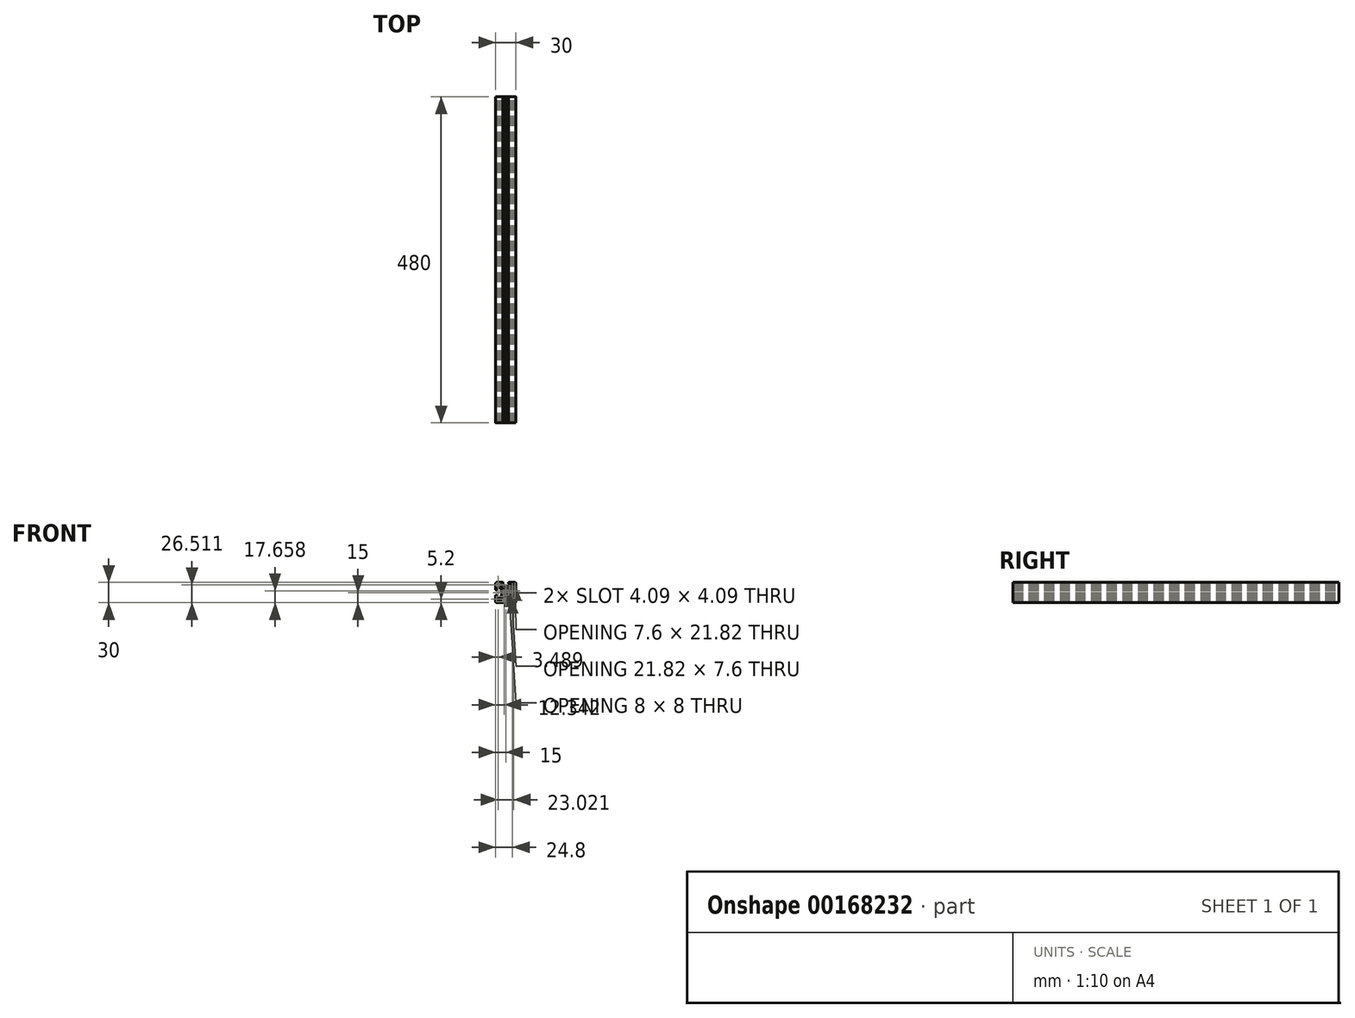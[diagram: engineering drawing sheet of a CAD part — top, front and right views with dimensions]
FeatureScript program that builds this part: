
annotation { "Feature Type Name" : "Feature", "Feature Type Description" : "" }
export const myFeature = defineFeature(function(context is Context, id is Id, definition is map)
    precondition{}
    {
        {
            var Q0;
            Q0=qCreatedBy(makeId("Front.planeOp"),FACE);
            var sketch = newSketch(context, id + "F0", { "sketchPlane" : qUnion([Q0])});
            skLineSegment(sketch, "E0", {"start": v(0, 17) * mm, "end": v(0, -17) * mm});
            skLineSegment(sketch, "E1", {"start": v(-17, 0) * mm, "end": v(17, 0) * mm});
            skLineSegment(sketch, "E2", {"start": v(-13, 15) * mm, "end": v(-4.3, 15) * mm});
            skLineSegment(sketch, "E3", {"start": v(-13, -15) * mm, "end": v(13, -15) * mm});
            skLineSegment(sketch, "E4", {"start": v(15, 13) * mm, "end": v(15, -13) * mm});
            skLineSegment(sketch, "E5", {"start": v(-15, 13) * mm, "end": v(-15, 4.3) * mm});
            skArc(sketch, "E6", {"start": v(15, 13) * mm, "mid": v(14.41, 14.41) * mm, "end": v(13, 15) * mm});
            skArc(sketch, "E7", {"start": v(-13, 15) * mm, "mid": v(-14.41, 14.41) * mm, "end": v(-15, 13) * mm});
            skArc(sketch, "E8", {"start": v(-15, -13) * mm, "mid": v(-14.41, -14.41) * mm, "end": v(-13, -15) * mm});
            skArc(sketch, "E9", {"start": v(13, -15) * mm, "mid": v(14.41, -14.41) * mm, "end": v(15, -13) * mm});
            skLineSegment(sketch, "E10", {"start": v(-13, -8.25) * mm, "end": v(-13, -4.3) * mm});
            skLineSegment(sketch, "E11", {"start": v(13, 8.19) * mm, "end": v(13, -7.25) * mm});
            skLineSegment(sketch, "E12", {"start": v(-8.19, -13) * mm, "end": v(7.25, -13) * mm});
            skLineSegment(sketch, "E13", {"start": v(-14.7, -4) * mm, "end": v(-13.3, -4) * mm});
            skLineSegment(sketch, "E14", {"start": v(-14.7, 4) * mm, "end": v(-13.3, 4) * mm});
            skLineSegment(sketch, "E15", {"start": v(-13, 4.3) * mm, "end": v(-13, 8.25) * mm});
            skLineSegment(sketch, "E16", {"start": v(4.3, 15) * mm, "end": v(13, 15) * mm});
            skLineSegment(sketch, "E17", {"start": v(-9.66, -8.25) * mm, "end": v(-13, -8.25) * mm});
            skLineSegment(sketch, "E18", {"start": v(-9.66, 8.25) * mm, "end": v(-13, 8.25) * mm});
            skLineSegment(sketch, "E19", {"start": v(4.59, 6) * mm, "end": v(0.65, 6) * mm});
            skLineSegment(sketch, "E20", {"start": v(4.17, -6) * mm, "end": v(-4.17, -6) * mm});
            skLineSegment(sketch, "E21", {"start": v(6, -4.17) * mm, "end": v(6, 4.17) * mm});
            skLineSegment(sketch, "E22", {"start": v(-6, -4.59) * mm, "end": v(-6, -2.5) * mm});
            skLineSegment(sketch, "E23", {"start": v(-4.59, 6) * mm, "end": v(-8.25, 9.66) * mm});
            skLineSegment(sketch, "E24", {"start": v(-6, 4.59) * mm, "end": v(-9.66, 8.25) * mm});
            skLineSegment(sketch, "E25", {"start": v(6.3, 4.88) * mm, "end": v(9.16, 7.74) * mm});
            skLineSegment(sketch, "E26", {"start": v(4.59, 6) * mm, "end": v(8.25, 9.66) * mm});
            skLineSegment(sketch, "E27", {"start": v(6.3, -4.88) * mm, "end": v(9.37, -7.96) * mm});
            skLineSegment(sketch, "E28", {"start": v(4.88, -6.3) * mm, "end": v(7.96, -9.37) * mm});
            skLineSegment(sketch, "E29", {"start": v(-4.88, -6.3) * mm, "end": v(-7.74, -9.16) * mm});
            skLineSegment(sketch, "E30", {"start": v(-6, -4.59) * mm, "end": v(-9.66, -8.25) * mm});
            skLineSegment(sketch, "E31", {"start": v(-15, -4.3) * mm, "end": v(-15, -13) * mm});
            skLineSegment(sketch, "E32", {"start": v(-4, 14.7) * mm, "end": v(-4, 13.3) * mm});
            skLineSegment(sketch, "E33", {"start": v(4, 14.7) * mm, "end": v(4, 13.3) * mm});
            skLineSegment(sketch, "E34", {"start": v(8.25, 9.66) * mm, "end": v(8.25, 13) * mm});
            skLineSegment(sketch, "E35", {"start": v(-8.25, 9.66) * mm, "end": v(-8.25, 13) * mm});
            skLineSegment(sketch, "E36", {"start": v(-4.3, 13) * mm, "end": v(-8.25, 13) * mm});
            skLineSegment(sketch, "E37", {"start": v(4.3, 13) * mm, "end": v(8.25, 13) * mm});
            skLineSegment(sketch, "E38", {"start": v(9.45, 8.45) * mm, "end": v(9.45, 11.07) * mm});
            skLineSegment(sketch, "E39", {"start": v(9.45, 11.07) * mm, "end": v(9.91, 12.35) * mm});
            skArc(sketch, "E40", {"start": v(12.78, 10.14) * mm, "mid": v(12.86, 13.2) * mm, "end": v(9.91, 12.35) * mm});
            skArc(sketch, "E41", {"start": v(12.78, 10.14) * mm, "mid": v(12.35, 9.27) * mm, "end": v(12.85, 8.45) * mm});
            skArc(sketch, "E42", {"start": v(13, 8.19) * mm, "mid": v(12.96, 8.34) * mm, "end": v(12.85, 8.45) * mm});
            skArc(sketch, "E43", {"start": v(-9.91, 12.35) * mm, "mid": v(-13.04, 13.04) * mm, "end": v(-12.35, 9.91) * mm});
            skLineSegment(sketch, "E44", {"start": v(-9.55, 11.34) * mm, "end": v(-9.91, 12.35) * mm});
            skLineSegment(sketch, "E45", {"start": v(-11.34, 9.55) * mm, "end": v(-12.35, 9.91) * mm});
            skArc(sketch, "E46", {"start": v(-11.34, 9.55) * mm, "mid": v(-9.87, 9.87) * mm, "end": v(-9.55, 11.34) * mm});
            skArc(sketch, "E47", {"start": v(9.91, -12.35) * mm, "mid": v(13.04, -13.04) * mm, "end": v(12.35, -9.91) * mm});
            skLineSegment(sketch, "E48", {"start": v(11.34, -9.55) * mm, "end": v(12.35, -9.91) * mm});
            skLineSegment(sketch, "E49", {"start": v(9.55, -11.34) * mm, "end": v(9.91, -12.35) * mm});
            skArc(sketch, "E50", {"start": v(11.34, -9.55) * mm, "mid": v(9.87, -9.87) * mm, "end": v(9.55, -11.34) * mm});
            skArc(sketch, "E51", {"start": v(6.3, 4.88) * mm, "mid": v(6.08, 4.55) * mm, "end": v(6, 4.17) * mm});
            skArc(sketch, "E52", {"start": v(6, -4.17) * mm, "mid": v(6.08, -4.55) * mm, "end": v(6.3, -4.88) * mm});
            skLineSegment(sketch, "E53", {"start": v(10.08, -8.25) * mm, "end": v(12, -8.25) * mm});
            skArc(sketch, "E54", {"start": v(9.37, -7.96) * mm, "mid": v(9.7, -8.17) * mm, "end": v(10.08, -8.25) * mm});
            skArc(sketch, "E55", {"start": v(12, -8.25) * mm, "mid": v(12.7, -7.96) * mm, "end": v(13, -7.25) * mm});
            skArc(sketch, "E56", {"start": v(9.16, 7.74) * mm, "mid": v(9.37, 8.07) * mm, "end": v(9.45, 8.45) * mm});
            skLineSegment(sketch, "E57", {"start": v(8.25, -10.08) * mm, "end": v(8.25, -12) * mm});
            skLineSegment(sketch, "E58", {"start": v(-8.45, -9.45) * mm, "end": v(-11.07, -9.45) * mm});
            skLineSegment(sketch, "E59", {"start": v(-11.07, -9.45) * mm, "end": v(-12.35, -9.91) * mm});
            skArc(sketch, "E60", {"start": v(-12.35, -9.91) * mm, "mid": v(-13.2, -12.86) * mm, "end": v(-10.14, -12.78) * mm});
            skArc(sketch, "E61", {"start": v(-8.45, -12.85) * mm, "mid": v(-9.27, -12.35) * mm, "end": v(-10.14, -12.78) * mm});
            skArc(sketch, "E62", {"start": v(-8.45, -12.85) * mm, "mid": v(-8.34, -12.96) * mm, "end": v(-8.19, -13) * mm});
            skArc(sketch, "E63", {"start": v(-8.45, -9.45) * mm, "mid": v(-8.07, -9.37) * mm, "end": v(-7.74, -9.16) * mm});
            skArc(sketch, "E64", {"start": v(-4.17, -6) * mm, "mid": v(-4.55, -6.08) * mm, "end": v(-4.88, -6.3) * mm});
            skArc(sketch, "E65", {"start": v(4.88, -6.3) * mm, "mid": v(4.55, -6.08) * mm, "end": v(4.17, -6) * mm});
            skArc(sketch, "E66", {"start": v(8.25, -10.08) * mm, "mid": v(8.17, -9.7) * mm, "end": v(7.96, -9.37) * mm});
            skArc(sketch, "E67", {"start": v(7.25, -13) * mm, "mid": v(7.96, -12.7) * mm, "end": v(8.25, -12) * mm});
            skLineSegment(sketch, "E68", {"start": v(3.5, 4) * mm, "end": v(2, 4) * mm});
            skLineSegment(sketch, "E69", {"start": v(4, -3.5) * mm, "end": v(4, -2) * mm});
            skLineSegment(sketch, "E70", {"start": v(3.5, -4) * mm, "end": v(2, -4) * mm});
            skLineSegment(sketch, "E71", {"start": v(-4, -3.5) * mm, "end": v(-4, -2) * mm});
            skLineSegment(sketch, "E72", {"start": v(-2.5, 6) * mm, "end": v(-1.22, 5.75) * mm});
            skLineSegment(sketch, "E73", {"start": v(0, 5.7) * mm, "end": v(-0.4, 5.93) * mm});
            skLineSegment(sketch, "E74", {"start": v(0, 5.7) * mm, "end": v(0.4, 5.93) * mm});
            skLineSegment(sketch, "E75", {"start": v(-2.5, 6) * mm, "end": v(-4.59, 6) * mm});
            skArc(sketch, "E76", {"start": v(0.65, 6) * mm, "mid": v(0.52, 5.98) * mm, "end": v(0.4, 5.93) * mm});
            skArc(sketch, "E77", {"start": v(-0.4, 5.93) * mm, "mid": v(-0.65, 6) * mm, "end": v(-0.9, 5.93) * mm});
            skLineSegment(sketch, "E78", {"start": v(-1.22, 5.75) * mm, "end": v(-0.9, 5.93) * mm});
            skArc(sketch, "E79", {"start": v(-6, 0.65) * mm, "mid": v(-5.98, 0.52) * mm, "end": v(-5.93, 0.4) * mm});
            skLineSegment(sketch, "E80", {"start": v(-6, -2.5) * mm, "end": v(-5.75, -1.22) * mm});
            skLineSegment(sketch, "E81", {"start": v(-5.7, 0) * mm, "end": v(-5.93, -0.4) * mm});
            skLineSegment(sketch, "E82", {"start": v(-5.7, 0) * mm, "end": v(-5.93, 0.4) * mm});
            skArc(sketch, "E83", {"start": v(-5.93, -0.4) * mm, "mid": v(-6, -0.65) * mm, "end": v(-5.93, -0.9) * mm});
            skLineSegment(sketch, "E84", {"start": v(-5.75, -1.22) * mm, "end": v(-5.93, -0.9) * mm});
            skLineSegment(sketch, "E85", {"start": v(-6, 0.65) * mm, "end": v(-6, 4.59) * mm});
            skArc(sketch, "E86", {"start": v(4, 13.3) * mm, "mid": v(4.09, 13.09) * mm, "end": v(4.3, 13) * mm});
            skArc(sketch, "E87", {"start": v(4.3, 15) * mm, "mid": v(4.09, 14.91) * mm, "end": v(4, 14.7) * mm});
            skArc(sketch, "E88", {"start": v(-4.3, 13) * mm, "mid": v(-4.09, 13.09) * mm, "end": v(-4, 13.3) * mm});
            skArc(sketch, "E89", {"start": v(-4, 14.7) * mm, "mid": v(-4.09, 14.91) * mm, "end": v(-4.3, 15) * mm});
            skArc(sketch, "E90", {"start": v(-13.3, 4) * mm, "mid": v(-13.09, 4.09) * mm, "end": v(-13, 4.3) * mm});
            skArc(sketch, "E91", {"start": v(-15, 4.3) * mm, "mid": v(-14.91, 4.09) * mm, "end": v(-14.7, 4) * mm});
            skArc(sketch, "E92", {"start": v(-13, -4.3) * mm, "mid": v(-13.09, -4.09) * mm, "end": v(-13.3, -4) * mm});
            skArc(sketch, "E93", {"start": v(-14.7, -4) * mm, "mid": v(-14.91, -4.09) * mm, "end": v(-15, -4.3) * mm});
            skArc(sketch, "E94", {"start": v(0.99, 3.25) * mm, "mid": v(0, 3.4) * mm, "end": v(-0.99, 3.25) * mm});
            skArc(sketch, "E95", {"start": v(-1.5, 3.58) * mm, "mid": v(-1.32, 3.3) * mm, "end": v(-0.99, 3.25) * mm});
            skArc(sketch, "E96", {"start": v(-1.5, 3.58) * mm, "mid": v(-1.67, 3.88) * mm, "end": v(-2, 4) * mm});
            skArc(sketch, "E97", {"start": v(0.99, 3.25) * mm, "mid": v(1.32, 3.3) * mm, "end": v(1.5, 3.58) * mm});
            skArc(sketch, "E98", {"start": v(2, 4) * mm, "mid": v(1.67, 3.88) * mm, "end": v(1.5, 3.58) * mm});
            skLineSegment(sketch, "E99", {"start": v(-2, 4) * mm, "end": v(-3.5, 4) * mm});
            skArc(sketch, "E100", {"start": v(-3.5, 4) * mm, "mid": v(-3.85, 3.85) * mm, "end": v(-4, 3.5) * mm});
            skArc(sketch, "E101", {"start": v(4, 3.5) * mm, "mid": v(3.85, 3.85) * mm, "end": v(3.5, 4) * mm});
            skArc(sketch, "E102", {"start": v(3.5, -4) * mm, "mid": v(3.85, -3.85) * mm, "end": v(4, -3.5) * mm});
            skArc(sketch, "E103", {"start": v(-4, -3.5) * mm, "mid": v(-3.85, -3.85) * mm, "end": v(-3.5, -4) * mm});
            skArc(sketch, "E104", {"start": v(-3.25, 0.99) * mm, "mid": v(-3.4, 0) * mm, "end": v(-3.25, -0.99) * mm});
            skArc(sketch, "E105", {"start": v(-3.58, -1.5) * mm, "mid": v(-3.3, -1.32) * mm, "end": v(-3.25, -0.99) * mm});
            skArc(sketch, "E106", {"start": v(-3.58, -1.5) * mm, "mid": v(-3.88, -1.67) * mm, "end": v(-4, -2) * mm});
            skArc(sketch, "E107", {"start": v(-3.25, 0.99) * mm, "mid": v(-3.3, 1.32) * mm, "end": v(-3.58, 1.5) * mm});
            skArc(sketch, "E108", {"start": v(-4, 2) * mm, "mid": v(-3.88, 1.67) * mm, "end": v(-3.58, 1.5) * mm});
            skArc(sketch, "E109", {"start": v(3.25, -0.99) * mm, "mid": v(3.4, 0) * mm, "end": v(3.25, 0.99) * mm});
            skArc(sketch, "E110", {"start": v(3.58, 1.5) * mm, "mid": v(3.3, 1.32) * mm, "end": v(3.25, 0.99) * mm});
            skArc(sketch, "E111", {"start": v(3.58, 1.5) * mm, "mid": v(3.88, 1.67) * mm, "end": v(4, 2) * mm});
            skArc(sketch, "E112", {"start": v(3.25, -0.99) * mm, "mid": v(3.3, -1.32) * mm, "end": v(3.58, -1.5) * mm});
            skArc(sketch, "E113", {"start": v(4, -2) * mm, "mid": v(3.88, -1.67) * mm, "end": v(3.58, -1.5) * mm});
            skArc(sketch, "E114", {"start": v(-0.99, -3.25) * mm, "mid": v(0, -3.4) * mm, "end": v(0.99, -3.25) * mm});
            skArc(sketch, "E115", {"start": v(-0.99, -3.25) * mm, "mid": v(-1.32, -3.3) * mm, "end": v(-1.5, -3.58) * mm});
            skArc(sketch, "E116", {"start": v(-2, -4) * mm, "mid": v(-1.67, -3.88) * mm, "end": v(-1.5, -3.58) * mm});
            skArc(sketch, "E117", {"start": v(1.5, -3.58) * mm, "mid": v(1.32, -3.3) * mm, "end": v(0.99, -3.25) * mm});
            skArc(sketch, "E118", {"start": v(1.5, -3.58) * mm, "mid": v(1.67, -3.88) * mm, "end": v(2, -4) * mm});
            skLineSegment(sketch, "E119", {"start": v(4, 2) * mm, "end": v(4, 3.5) * mm});
            skLineSegment(sketch, "E120", {"start": v(-2, -4) * mm, "end": v(-3.5, -4) * mm});
            skLineSegment(sketch, "E121", {"start": v(-4, 2) * mm, "end": v(-4, 3.5) * mm});
            skCircle(sketch, "E122", {"center": v(0, 0) * mm, "radius": 3.4 * mm});
            skLineSegment(sketch, "E123", {"start": v(11.7, 15.6) * mm, "end": v(11.7, 7.8) * mm});
            skLineSegment(sketch, "E124", {"start": v(7.8, 11.7) * mm, "end": v(15.6, 11.7) * mm});
            skLineSegment(sketch, "E125", {"start": v(11.7, -7.8) * mm, "end": v(11.7, -15.6) * mm});
            skLineSegment(sketch, "E126", {"start": v(7.8, -11.7) * mm, "end": v(15.6, -11.7) * mm});
            skLineSegment(sketch, "E127", {"start": v(-11.7, -7.8) * mm, "end": v(-11.7, -15.6) * mm});
            skLineSegment(sketch, "E128", {"start": v(-15.6, -11.7) * mm, "end": v(-7.8, -11.7) * mm});
            skLineSegment(sketch, "E129", {"start": v(-11.7, 15.6) * mm, "end": v(-11.7, 7.8) * mm});
            skLineSegment(sketch, "E130", {"start": v(-15.6, 11.7) * mm, "end": v(-7.8, 11.7) * mm});
            skSolve(sketch);
        }
        {
            var Q0;
            Q0=qCreatedBy(makeId("Front.planeOp"),FACE);
            var sketch = newSketch(context, id + "F1", { "sketchPlane" : qUnion([Q0])});
            skArc(sketch, "E131.0", {"start": v(-8.45, -12.85) * mm, "mid": v(-9.27, -12.35) * mm, "end": v(-10.14, -12.78) * mm});
            skLineSegment(sketch, "E131.1", {"start": v(-4.88, -6.3) * mm, "end": v(-7.74, -9.16) * mm});
            skLineSegment(sketch, "E131.3", {"start": v(4.17, -6) * mm, "end": v(-4.17, -6) * mm});
            skLineSegment(sketch, "E131.4", {"start": v(-4.3, 13) * mm, "end": v(-8.25, 13) * mm});
            skArc(sketch, "E131.5", {"start": v(-11.34, 9.55) * mm, "mid": v(-9.87, 9.87) * mm, "end": v(-9.55, 11.34) * mm});
            skLineSegment(sketch, "E131.6", {"start": v(-6, -4.59) * mm, "end": v(-9.66, -8.25) * mm});
            skLineSegment(sketch, "E131.7", {"start": v(6, -4.17) * mm, "end": v(6, 4.17) * mm});
            skLineSegment(sketch, "E131.8", {"start": v(-6, 0.65) * mm, "end": v(-6, 4.59) * mm});
            skLineSegment(sketch, "E131.9", {"start": v(4.3, 13) * mm, "end": v(8.25, 13) * mm});
            skLineSegment(sketch, "E131.10", {"start": v(-6, -4.59) * mm, "end": v(-6, -2.5) * mm});
            skLineSegment(sketch, "E131.11", {"start": v(9.45, 8.45) * mm, "end": v(9.45, 11.07) * mm});
            skLineSegment(sketch, "E131.12", {"start": v(-4.59, 6) * mm, "end": v(-8.25, 9.66) * mm});
            skLineSegment(sketch, "E131.13", {"start": v(-8.25, 9.66) * mm, "end": v(-8.25, 13) * mm});
            skLineSegment(sketch, "E131.15", {"start": v(8.25, 9.66) * mm, "end": v(8.25, 13) * mm});
            skArc(sketch, "E131.16", {"start": v(11.34, -9.55) * mm, "mid": v(9.87, -9.87) * mm, "end": v(9.55, -11.34) * mm});
            skLineSegment(sketch, "E131.17", {"start": v(-9.66, 8.25) * mm, "end": v(-13, 8.25) * mm});
            skLineSegment(sketch, "E131.18", {"start": v(4.59, 6) * mm, "end": v(0.65, 6) * mm});
            skLineSegment(sketch, "E131.19", {"start": v(-8.19, -13) * mm, "end": v(7.25, -13) * mm});
            skLineSegment(sketch, "E131.20", {"start": v(13, 8.19) * mm, "end": v(13, -7.25) * mm});
            skLineSegment(sketch, "E131.21", {"start": v(-13, -8.25) * mm, "end": v(-13, -4.3) * mm});
            skArc(sketch, "E131.23", {"start": v(13, -15) * mm, "mid": v(14.41, -14.41) * mm, "end": v(15, -13) * mm});
            skArc(sketch, "E131.24", {"start": v(-15, -13) * mm, "mid": v(-14.41, -14.41) * mm, "end": v(-13, -15) * mm});
            skArc(sketch, "E131.25", {"start": v(-13, 15) * mm, "mid": v(-14.41, 14.41) * mm, "end": v(-15, 13) * mm});
            skArc(sketch, "E131.26", {"start": v(15, 13) * mm, "mid": v(14.41, 14.41) * mm, "end": v(13, 15) * mm});
            skLineSegment(sketch, "E131.27", {"start": v(-15, 13) * mm, "end": v(-15, 4.3) * mm});
            skLineSegment(sketch, "E131.28", {"start": v(15, 13) * mm, "end": v(15, -13) * mm});
            skLineSegment(sketch, "E131.29", {"start": v(-9.66, -8.25) * mm, "end": v(-13, -8.25) * mm});
            skLineSegment(sketch, "E131.30", {"start": v(-13, -15) * mm, "end": v(13, -15) * mm});
            skLineSegment(sketch, "E131.31", {"start": v(-13, 15) * mm, "end": v(-4.3, 15) * mm});
            skLineSegment(sketch, "E131.32", {"start": v(-13, 4.3) * mm, "end": v(-13, 8.25) * mm});
            skLineSegment(sketch, "E131.33", {"start": v(4.88, -6.3) * mm, "end": v(7.96, -9.37) * mm});
            skArc(sketch, "E131.34", {"start": v(-12.35, -9.91) * mm, "mid": v(-13.2, -12.86) * mm, "end": v(-10.14, -12.78) * mm});
            skLineSegment(sketch, "E131.35", {"start": v(-2.5, 6) * mm, "end": v(-4.59, 6) * mm});
            skLineSegment(sketch, "E131.37", {"start": v(6.3, -4.88) * mm, "end": v(9.37, -7.96) * mm});
            skArc(sketch, "E131.38", {"start": v(-9.91, 12.35) * mm, "mid": v(-13.04, 13.04) * mm, "end": v(-12.35, 9.91) * mm});
            skLineSegment(sketch, "E131.39", {"start": v(4.3, 15) * mm, "end": v(13, 15) * mm});
            skLineSegment(sketch, "E131.41", {"start": v(4.59, 6) * mm, "end": v(8.25, 9.66) * mm});
            skLineSegment(sketch, "E131.42", {"start": v(-8.45, -9.45) * mm, "end": v(-11.07, -9.45) * mm});
            skLineSegment(sketch, "E131.43", {"start": v(6.3, 4.88) * mm, "end": v(9.16, 7.74) * mm});
            skLineSegment(sketch, "E131.46", {"start": v(-15, -4.3) * mm, "end": v(-15, -13) * mm});
            skArc(sketch, "E131.47", {"start": v(9.91, -12.35) * mm, "mid": v(13.04, -13.04) * mm, "end": v(12.35, -9.91) * mm});
            skLineSegment(sketch, "E131.48", {"start": v(-6, 4.59) * mm, "end": v(-9.66, 8.25) * mm});
            skArc(sketch, "E131.49", {"start": v(12.78, 10.14) * mm, "mid": v(12.86, 13.2) * mm, "end": v(9.91, 12.35) * mm});
            skArc(sketch, "E131.50", {"start": v(3.25, -0.99) * mm, "mid": v(3.4, 0) * mm, "end": v(3.25, 0.99) * mm});
            skArc(sketch, "E131.51", {"start": v(0.99, 3.25) * mm, "mid": v(0, 3.4) * mm, "end": v(-0.99, 3.25) * mm});
            skArc(sketch, "E131.52", {"start": v(-0.99, -3.25) * mm, "mid": v(0, -3.4) * mm, "end": v(0.99, -3.25) * mm});
            skLineSegment(sketch, "E131.53", {"start": v(8.25, -10.08) * mm, "end": v(8.25, -12) * mm});
            skArc(sketch, "E131.54", {"start": v(-3.25, 0.99) * mm, "mid": v(-3.4, 0) * mm, "end": v(-3.25, -0.99) * mm});
            skArc(sketch, "E131.55", {"start": v(-0.99, -3.25) * mm, "mid": v(-1.32, -3.3) * mm, "end": v(-1.5, -3.58) * mm});
            skLineSegment(sketch, "E131.56", {"start": v(-11.34, 9.55) * mm, "end": v(-12.35, 9.91) * mm});
            skLineSegment(sketch, "E131.57", {"start": v(-2, 4) * mm, "end": v(-3.5, 4) * mm});
            skLineSegment(sketch, "E131.58", {"start": v(3.5, 4) * mm, "end": v(2, 4) * mm});
            skArc(sketch, "E131.59", {"start": v(6, -4.17) * mm, "mid": v(6.08, -4.55) * mm, "end": v(6.3, -4.88) * mm});
            skArc(sketch, "E131.60", {"start": v(-2, -4) * mm, "mid": v(-1.67, -3.88) * mm, "end": v(-1.5, -3.58) * mm});
            skArc(sketch, "E131.61", {"start": v(-3.5, 4) * mm, "mid": v(-3.85, 3.85) * mm, "end": v(-4, 3.5) * mm});
            skArc(sketch, "E131.62", {"start": v(3.58, 1.5) * mm, "mid": v(3.3, 1.32) * mm, "end": v(3.25, 0.99) * mm});
            skLineSegment(sketch, "E131.63", {"start": v(4, -3.5) * mm, "end": v(4, -2) * mm});
            skLineSegment(sketch, "E131.64", {"start": v(10.08, -8.25) * mm, "end": v(12, -8.25) * mm});
            skArc(sketch, "E131.65", {"start": v(1.5, -3.58) * mm, "mid": v(1.32, -3.3) * mm, "end": v(0.99, -3.25) * mm});
            skArc(sketch, "E131.66", {"start": v(4, 3.5) * mm, "mid": v(3.85, 3.85) * mm, "end": v(3.5, 4) * mm});
            skArc(sketch, "E131.67", {"start": v(4, 13.3) * mm, "mid": v(4.09, 13.09) * mm, "end": v(4.3, 13) * mm});
            skLineSegment(sketch, "E131.68", {"start": v(3.5, -4) * mm, "end": v(2, -4) * mm});
            skArc(sketch, "E131.69", {"start": v(9.37, -7.96) * mm, "mid": v(9.7, -8.17) * mm, "end": v(10.08, -8.25) * mm});
            skArc(sketch, "E131.70", {"start": v(1.5, -3.58) * mm, "mid": v(1.67, -3.88) * mm, "end": v(2, -4) * mm});
            skArc(sketch, "E131.71", {"start": v(3.5, -4) * mm, "mid": v(3.85, -3.85) * mm, "end": v(4, -3.5) * mm});
            skArc(sketch, "E131.72", {"start": v(12, -8.25) * mm, "mid": v(12.7, -7.96) * mm, "end": v(13, -7.25) * mm});
            skLineSegment(sketch, "E131.73", {"start": v(9.45, 11.07) * mm, "end": v(9.91, 12.35) * mm});
            skLineSegment(sketch, "E131.74", {"start": v(4, 2) * mm, "end": v(4, 3.5) * mm});
            skArc(sketch, "E131.75", {"start": v(-4, -3.5) * mm, "mid": v(-3.85, -3.85) * mm, "end": v(-3.5, -4) * mm});
            skArc(sketch, "E131.76", {"start": v(4.3, 15) * mm, "mid": v(4.09, 14.91) * mm, "end": v(4, 14.7) * mm});
            skLineSegment(sketch, "E131.77", {"start": v(-4, -3.5) * mm, "end": v(-4, -2) * mm});
            skArc(sketch, "E131.78", {"start": v(8.25, -10.08) * mm, "mid": v(8.17, -9.7) * mm, "end": v(7.96, -9.37) * mm});
            skArc(sketch, "E131.79", {"start": v(-8.45, -9.45) * mm, "mid": v(-8.07, -9.37) * mm, "end": v(-7.74, -9.16) * mm});
            skArc(sketch, "E131.80", {"start": v(6.3, 4.88) * mm, "mid": v(6.08, 4.55) * mm, "end": v(6, 4.17) * mm});
            skArc(sketch, "E131.81", {"start": v(7.25, -13) * mm, "mid": v(7.96, -12.7) * mm, "end": v(8.25, -12) * mm});
            skLineSegment(sketch, "E131.82", {"start": v(4, 14.7) * mm, "end": v(4, 13.3) * mm});
            skLineSegment(sketch, "E131.83", {"start": v(9.55, -11.34) * mm, "end": v(9.91, -12.35) * mm});
            skArc(sketch, "E131.84", {"start": v(4.88, -6.3) * mm, "mid": v(4.55, -6.08) * mm, "end": v(4.17, -6) * mm});
            skArc(sketch, "E131.85", {"start": v(0.65, 6) * mm, "mid": v(0.52, 5.98) * mm, "end": v(0.4, 5.93) * mm});
            skArc(sketch, "E131.86", {"start": v(-4, 2) * mm, "mid": v(-3.88, 1.67) * mm, "end": v(-3.58, 1.5) * mm});
            skLineSegment(sketch, "E131.87", {"start": v(-9.55, 11.34) * mm, "end": v(-9.91, 12.35) * mm});
            skArc(sketch, "E131.88", {"start": v(-3.25, 0.99) * mm, "mid": v(-3.3, 1.32) * mm, "end": v(-3.58, 1.5) * mm});
            skLineSegment(sketch, "E131.89", {"start": v(-11.07, -9.45) * mm, "end": v(-12.35, -9.91) * mm});
            skLineSegment(sketch, "E131.90", {"start": v(11.34, -9.55) * mm, "end": v(12.35, -9.91) * mm});
            skArc(sketch, "E131.91", {"start": v(-4.17, -6) * mm, "mid": v(-4.55, -6.08) * mm, "end": v(-4.88, -6.3) * mm});
            skLineSegment(sketch, "E131.92", {"start": v(-6, -2.5) * mm, "end": v(-5.75, -1.22) * mm});
            skArc(sketch, "E131.93", {"start": v(13, 8.19) * mm, "mid": v(12.96, 8.34) * mm, "end": v(12.85, 8.45) * mm});
            skLineSegment(sketch, "E131.94", {"start": v(-4, 2) * mm, "end": v(-4, 3.5) * mm});
            skArc(sketch, "E131.95", {"start": v(12.78, 10.14) * mm, "mid": v(12.35, 9.27) * mm, "end": v(12.85, 8.45) * mm});
            skArc(sketch, "E131.96", {"start": v(3.58, 1.5) * mm, "mid": v(3.88, 1.67) * mm, "end": v(4, 2) * mm});
            skLineSegment(sketch, "E131.97", {"start": v(-2.5, 6) * mm, "end": v(-1.22, 5.75) * mm});
            skLineSegment(sketch, "E131.98", {"start": v(-2, -4) * mm, "end": v(-3.5, -4) * mm});
            skArc(sketch, "E131.99", {"start": v(9.16, 7.74) * mm, "mid": v(9.37, 8.07) * mm, "end": v(9.45, 8.45) * mm});
            skArc(sketch, "E131.100", {"start": v(-0.4, 5.93) * mm, "mid": v(-0.65, 6) * mm, "end": v(-0.9, 5.93) * mm});
            skLineSegment(sketch, "E131.101", {"start": v(-5.75, -1.22) * mm, "end": v(-5.93, -0.9) * mm});
            skLineSegment(sketch, "E131.102", {"start": v(-1.22, 5.75) * mm, "end": v(-0.9, 5.93) * mm});
            skArc(sketch, "E131.103", {"start": v(-8.45, -12.85) * mm, "mid": v(-8.34, -12.96) * mm, "end": v(-8.19, -13) * mm});
            skArc(sketch, "E131.104", {"start": v(2, 4) * mm, "mid": v(1.67, 3.88) * mm, "end": v(1.5, 3.58) * mm});
            skArc(sketch, "E131.105", {"start": v(0.99, 3.25) * mm, "mid": v(1.32, 3.3) * mm, "end": v(1.5, 3.58) * mm});
            skArc(sketch, "E131.106", {"start": v(4, -2) * mm, "mid": v(3.88, -1.67) * mm, "end": v(3.58, -1.5) * mm});
            skLineSegment(sketch, "E131.107", {"start": v(-14.7, 4) * mm, "end": v(-13.3, 4) * mm});
            skArc(sketch, "E131.108", {"start": v(-15, 4.3) * mm, "mid": v(-14.91, 4.09) * mm, "end": v(-14.7, 4) * mm});
            skLineSegment(sketch, "E131.109", {"start": v(0, 5.7) * mm, "end": v(0.4, 5.93) * mm});
            skArc(sketch, "E131.110", {"start": v(-13.3, 4) * mm, "mid": v(-13.09, 4.09) * mm, "end": v(-13, 4.3) * mm});
            skArc(sketch, "E131.111", {"start": v(-3.58, -1.5) * mm, "mid": v(-3.88, -1.67) * mm, "end": v(-4, -2) * mm});
            skArc(sketch, "E131.112", {"start": v(-1.5, 3.58) * mm, "mid": v(-1.67, 3.88) * mm, "end": v(-2, 4) * mm});
            skLineSegment(sketch, "E131.113", {"start": v(0, 5.7) * mm, "end": v(-0.4, 5.93) * mm});
            skArc(sketch, "E131.114", {"start": v(-3.58, -1.5) * mm, "mid": v(-3.3, -1.32) * mm, "end": v(-3.25, -0.99) * mm});
            skArc(sketch, "E131.115", {"start": v(3.25, -0.99) * mm, "mid": v(3.3, -1.32) * mm, "end": v(3.58, -1.5) * mm});
            skArc(sketch, "E131.116", {"start": v(-1.5, 3.58) * mm, "mid": v(-1.32, 3.3) * mm, "end": v(-0.99, 3.25) * mm});
            skLineSegment(sketch, "E131.117", {"start": v(-5.7, 0) * mm, "end": v(-5.93, 0.4) * mm});
            skArc(sketch, "E131.118", {"start": v(-5.93, -0.4) * mm, "mid": v(-6, -0.65) * mm, "end": v(-5.93, -0.9) * mm});
            skLineSegment(sketch, "E131.119", {"start": v(-4, 14.7) * mm, "end": v(-4, 13.3) * mm});
            skArc(sketch, "E131.120", {"start": v(-4, 14.7) * mm, "mid": v(-4.09, 14.91) * mm, "end": v(-4.3, 15) * mm});
            skArc(sketch, "E131.121", {"start": v(-4.3, 13) * mm, "mid": v(-4.09, 13.09) * mm, "end": v(-4, 13.3) * mm});
            skArc(sketch, "E131.122", {"start": v(-14.7, -4) * mm, "mid": v(-14.91, -4.09) * mm, "end": v(-15, -4.3) * mm});
            skArc(sketch, "E131.123", {"start": v(-6, 0.65) * mm, "mid": v(-5.98, 0.52) * mm, "end": v(-5.93, 0.4) * mm});
            skLineSegment(sketch, "E131.124", {"start": v(-5.7, 0) * mm, "end": v(-5.93, -0.4) * mm});
            skLineSegment(sketch, "E131.125", {"start": v(-14.7, -4) * mm, "end": v(-13.3, -4) * mm});
            skArc(sketch, "E131.126", {"start": v(-13, -4.3) * mm, "mid": v(-13.09, -4.09) * mm, "end": v(-13.3, -4) * mm});
            skSolve(sketch);
        }
        {
            var Q0;
            Q0=makeQuery(id+"F1.imprint","IMPRINT",FACE,{"disambiguationData":[TD([[makeQuery(id+"F1.imprint","IMPRINT",EDGE,{"derivedFrom":sQuery(id+"F1.wireOp",EDGE,"E131.0")}),1.0]])]});
            extrude(context, id + "F2", {"entities" : qUnion([Q0]), "endBound" : BoundingType.SYMMETRIC, "depth" : 480 * mm});
        }
        {
            var Q0;
            Q0=qCreatedBy(makeId("Front.planeOp"),FACE);
            cPlane(context, id + "F3", {"entities" : qUnion([Q0]), "cplaneType" : CPlaneType.OFFSET, "offset" : 240 * mm, "oppositeDirection" : true, "width" : 150 * mm, "height" : 150 * mm});
        }
        {
            var Q0;
            Q0=qCreatedBy(id+"F3.planeOp",FACE);
            var sketch = newSketch(context, id + "F4", { "sketchPlane" : qUnion([Q0])});
            skLineSegment(sketch, "E132.0", {"start": v(-15, 13) * mm, "end": v(-15, 4.3) * mm});
            skLineSegment(sketch, "E133.0", {"start": v(-15, -4.3) * mm, "end": v(-15, -13) * mm});
            skLineSegment(sketch, "E134.0", {"start": v(-13, 15) * mm, "end": v(-4.3, 15) * mm});
            skLineSegment(sketch, "E135.0", {"start": v(4.3, 15) * mm, "end": v(13, 15) * mm});
            skLineSegment(sketch, "E136", {"start": v(-15, 4.3) * mm, "end": v(-15, -4.3) * mm, "construction": true});
            skLineSegment(sketch, "E137", {"start": v(-4.3, 15) * mm, "end": v(4.3, 15) * mm, "construction": true});
            skSolve(sketch);
        }
    });
